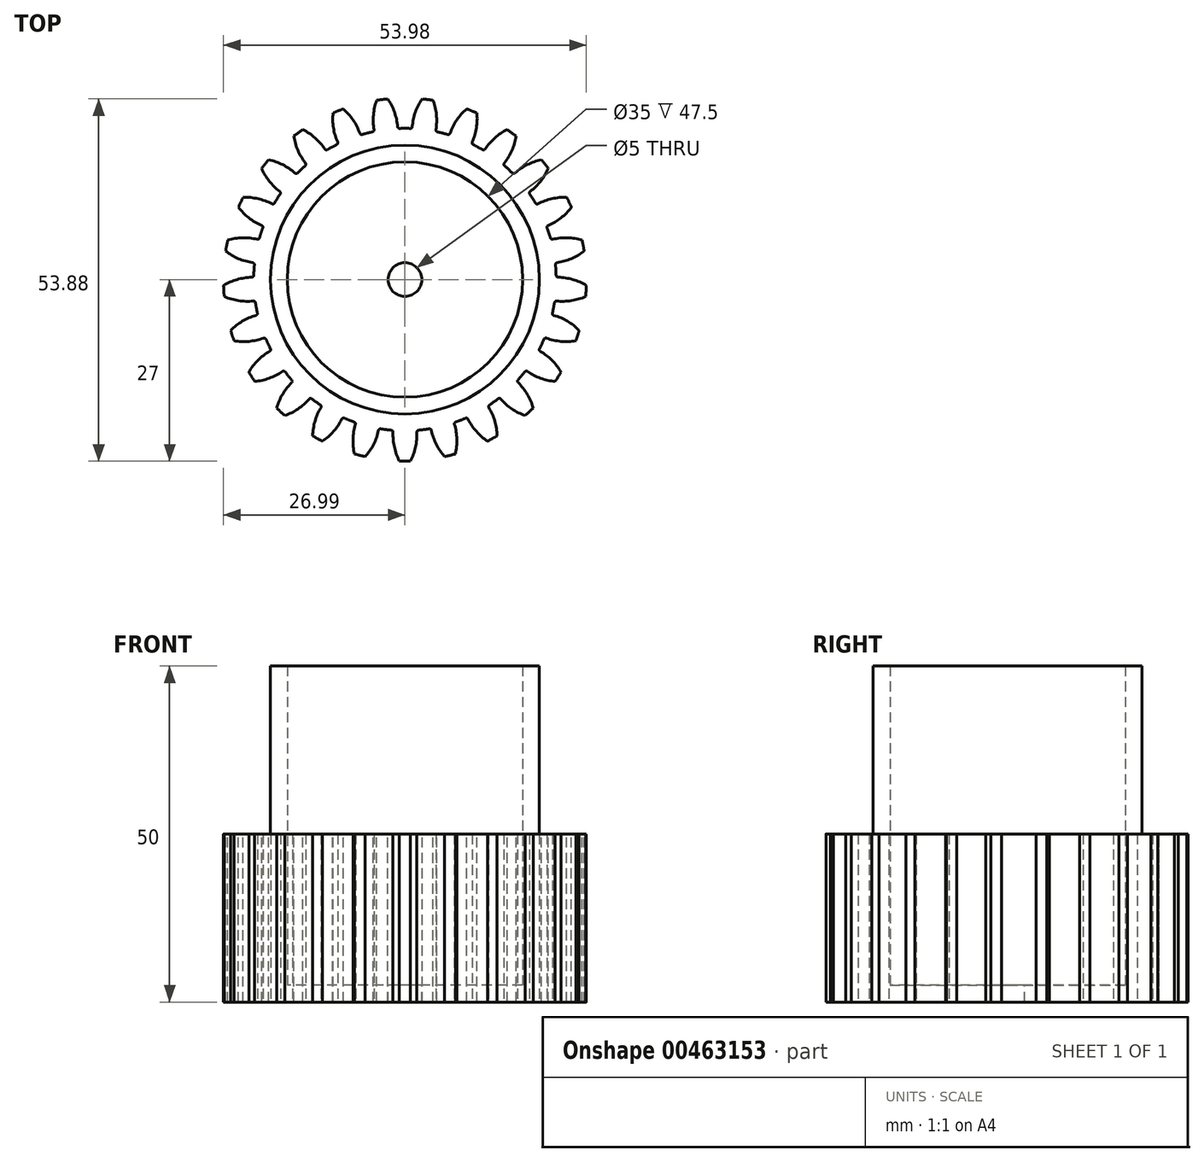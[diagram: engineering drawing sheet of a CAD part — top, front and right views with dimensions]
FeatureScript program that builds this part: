
annotation { "Feature Type Name" : "Feature", "Feature Type Description" : "" }
export const myFeature = defineFeature(function(context is Context, id is Id, definition is map)
    precondition{}
    {
        {
            var Q0;
            Q0=qCreatedBy(makeId("Top.planeOp"),FACE);
            var sketch = newSketch(context, id + "F0", { "sketchPlane" : qUnion([Q0])});
            skCircle(sketch, "E0", {"center": v(0, 0) * mm, "radius": 25 * mm});
            skCircle(sketch, "E1", {"center": v(0, 0) * mm, "radius": 27 * mm});
            skCircle(sketch, "E2", {"center": v(0, 0) * mm, "radius": 22.5 * mm});
            skSolve(sketch);
        }
        {
            var Q0;
            Q0=makeQuery(id+"F0.imprint","IMPRINT",FACE,{"disambiguationData":[TD([[makeQuery(id+"F0.imprint","IMPRINT",EDGE,{"derivedFrom":sQuery(id+"F0.wireOp",EDGE,"E2")}),1.0]])]});
            var Q1;
            Q1=makeQuery(id+"F0.imprint","IMPRINT",FACE,{"disambiguationData":[TD([[makeQuery(id+"F0.imprint","IMPRINT",EDGE,{"derivedFrom":sQuery(id+"F0.wireOp",EDGE,"E0")}),1.0]])]});
            var Q2;
            Q2=makeQuery(id+"F0.imprint","IMPRINT",FACE,{"disambiguationData":[TD([[makeQuery(id+"F0.imprint","IMPRINT",EDGE,{"derivedFrom":sQuery(id+"F0.wireOp",EDGE,"E0")}),-1.0]])]});
            extrude(context, id + "F1", {"entities" : qUnion([Q0, Q1, Q2]), "endBound" : BoundingType.SYMMETRIC, "depth" : 25 * mm});
        }
        {
            var Q0;
            Q0=qCreatedBy(makeId("Top.planeOp"),FACE);
            var sketch = newSketch(context, id + "F2", { "sketchPlane" : qUnion([Q0])});
            skLineSegment(sketch, "E3", {"start": v(0, 0) * mm, "end": v(0, 27) * mm, "construction": true});
            skArc(sketch, "E4", {"start": v(-1.07, 22.47) * mm, "mid": v(-1.72, 25.34) * mm, "end": v(-3.32, 27.8) * mm});
            skArc(sketch, "E5.MirrorCS", {"start": v(1.07, 22.47) * mm, "mid": v(1.72, 25.34) * mm, "end": v(3.32, 27.8) * mm});
            skArc(sketch, "E6.0", {"start": v(1.07, 22.47) * mm, "mid": v(0, 22.5) * mm, "end": v(-1.07, 22.47) * mm});
            skArc(sketch, "E7.0", {"start": v(3.32, 27.8) * mm, "mid": v(0, 28) * mm, "end": v(-3.32, 27.8) * mm});
            skLineSegment(sketch, "E8", {"start": v(-1.57, 24.95) * mm, "end": v(1.57, 24.95) * mm, "construction": true});
            skLineSegment(sketch, "E9", {"start": v(-1.07, 22.47) * mm, "end": v(0, 0) * mm, "construction": true});
            skLineSegment(sketch, "E10", {"start": v(0, 20.64) * mm, "end": v(-3.75, 30.95) * mm, "construction": true});
            skLineSegment(sketch, "E11", {"start": v(0, 0) * mm, "end": v(3.38, 26.79) * mm, "construction": true});
            skLineSegment(sketch, "E12", {"start": v(1.57, 24.95) * mm, "end": v(4.68, 24.56) * mm, "construction": true});
            skSolve(sketch);
        }
        {
            var Q0;
            Q0=makeQuery(id+"F2.imprint","IMPRINT",FACE,{"disambiguationData":[TD([[makeQuery(id+"F2.imprint","IMPRINT",EDGE,{"derivedFrom":sQuery(id+"F2.wireOp",EDGE,"E4")}),-1.0]])]});
            extrude(context, id + "F3", {"entities" : qUnion([Q0]), "operationType" : NewBodyOperationType.REMOVE, "endBound" : BoundingType.THROUGH_ALL, "oppositeDirection" : true, "depth" : 25 * mm, "hasSecondDirection" : true, "secondDirectionBound" : SecondDirectionBoundingType.THROUGH_ALL, "secondDirectionOppositeDirection" : false, "secondDirectionDepth" : 25 * mm});
        }
        {
            var Q0;
            Q0=makeQuery(id+"F3.boolean.opBoolean","COPY",EDGE,{"derivedFrom":makeQuery(id+"F3.opExtrude","SWEPT_EDGE",EDGE,{"disambiguationData":[OSD([sQuery(id+"F2.wireOp",EDGE,"E4"),sQuery(id+"F2.wireOp",EDGE,"E6.0")])]})});
            var Q1;
            Q1=makeQuery(id+"F3.boolean.opBoolean","COPY",EDGE,{"derivedFrom":makeQuery(id+"F3.opExtrude","SWEPT_EDGE",EDGE,{"disambiguationData":[OSD([sQuery(id+"F2.wireOp",EDGE,"E5.MirrorCS"),sQuery(id+"F2.wireOp",EDGE,"E6.0")])]})});
            fillet(context, id + "F4", {"entities" : qUnion([Q0, Q1]), "radius" : .3 * mm, "tangentPropagation" : true, "allowEdgeOverflow" : false});
        }
        {
            var Q0;
            Q0=qCreatedBy(makeId("Front.planeOp"),FACE);
            var sketch = newSketch(context, id + "F5", { "sketchPlane" : qUnion([Q0])});
            skLineSegment(sketch, "E13", {"start": v(0, 20.26) * mm, "end": v(0, -19.1) * mm, "construction": true});
            skSolve(sketch);
        }
        {
            var Q0;
            Q0=makeQuery(id+"F1.opExtrude","SWEPT_BODY",BODY,{"disambiguationData":[OSD([sQuery(id+"F0.wireOp",EDGE,"E1")])]});
            var Q1;
            Q1=sQuery(id+"F5.wireOp",EDGE,"E13");
            circularPattern(context, id + "F6", {"entities" : qUnion([Q0]), "axis" : qUnion([Q1]), "angle" : 360 * degree, "instanceCount" : 25, "equalSpace" : true});
        }
        {
            var Q0;
            Q0=makeQuery(id+"F1.opExtrude","SWEPT_BODY",BODY,{"disambiguationData":[OSD([sQuery(id+"F0.wireOp",EDGE,"E1")])]});
            var Q1;
            Q1=makeQuery(id+"F6.opPattern","COPY",BODY,{"derivedFrom":makeQuery(id+"F1.opExtrude","SWEPT_BODY",BODY,{"disambiguationData":[OSD([sQuery(id+"F0.wireOp",EDGE,"E1")])]}),"instanceName":"24"});
            var Q2;
            Q2=makeQuery(id+"F6.opPattern","COPY",BODY,{"derivedFrom":makeQuery(id+"F1.opExtrude","SWEPT_BODY",BODY,{"disambiguationData":[OSD([sQuery(id+"F0.wireOp",EDGE,"E1")])]}),"instanceName":"3"});
            var Q3;
            Q3=makeQuery(id+"F6.opPattern","COPY",BODY,{"derivedFrom":makeQuery(id+"F1.opExtrude","SWEPT_BODY",BODY,{"disambiguationData":[OSD([sQuery(id+"F0.wireOp",EDGE,"E1")])]}),"instanceName":"1"});
            var Q4;
            Q4=makeQuery(id+"F6.opPattern","COPY",BODY,{"derivedFrom":makeQuery(id+"F1.opExtrude","SWEPT_BODY",BODY,{"disambiguationData":[OSD([sQuery(id+"F0.wireOp",EDGE,"E1")])]}),"instanceName":"22"});
            var Q5;
            Q5=makeQuery(id+"F6.opPattern","COPY",BODY,{"derivedFrom":makeQuery(id+"F1.opExtrude","SWEPT_BODY",BODY,{"disambiguationData":[OSD([sQuery(id+"F0.wireOp",EDGE,"E1")])]}),"instanceName":"21"});
            var Q6;
            Q6=makeQuery(id+"F6.opPattern","COPY",BODY,{"derivedFrom":makeQuery(id+"F1.opExtrude","SWEPT_BODY",BODY,{"disambiguationData":[OSD([sQuery(id+"F0.wireOp",EDGE,"E1")])]}),"instanceName":"19"});
            var Q7;
            Q7=makeQuery(id+"F6.opPattern","COPY",BODY,{"derivedFrom":makeQuery(id+"F1.opExtrude","SWEPT_BODY",BODY,{"disambiguationData":[OSD([sQuery(id+"F0.wireOp",EDGE,"E1")])]}),"instanceName":"18"});
            var Q8;
            Q8=makeQuery(id+"F6.opPattern","COPY",BODY,{"derivedFrom":makeQuery(id+"F1.opExtrude","SWEPT_BODY",BODY,{"disambiguationData":[OSD([sQuery(id+"F0.wireOp",EDGE,"E1")])]}),"instanceName":"17"});
            var Q9;
            Q9=makeQuery(id+"F6.opPattern","COPY",BODY,{"derivedFrom":makeQuery(id+"F1.opExtrude","SWEPT_BODY",BODY,{"disambiguationData":[OSD([sQuery(id+"F0.wireOp",EDGE,"E1")])]}),"instanceName":"16"});
            var Q10;
            Q10=makeQuery(id+"F6.opPattern","COPY",BODY,{"derivedFrom":makeQuery(id+"F1.opExtrude","SWEPT_BODY",BODY,{"disambiguationData":[OSD([sQuery(id+"F0.wireOp",EDGE,"E1")])]}),"instanceName":"15"});
            var Q11;
            Q11=makeQuery(id+"F6.opPattern","COPY",BODY,{"derivedFrom":makeQuery(id+"F1.opExtrude","SWEPT_BODY",BODY,{"disambiguationData":[OSD([sQuery(id+"F0.wireOp",EDGE,"E1")])]}),"instanceName":"14"});
            var Q12;
            Q12=makeQuery(id+"F6.opPattern","COPY",BODY,{"derivedFrom":makeQuery(id+"F1.opExtrude","SWEPT_BODY",BODY,{"disambiguationData":[OSD([sQuery(id+"F0.wireOp",EDGE,"E1")])]}),"instanceName":"13"});
            var Q13;
            Q13=makeQuery(id+"F6.opPattern","COPY",BODY,{"derivedFrom":makeQuery(id+"F1.opExtrude","SWEPT_BODY",BODY,{"disambiguationData":[OSD([sQuery(id+"F0.wireOp",EDGE,"E1")])]}),"instanceName":"12"});
            var Q14;
            Q14=makeQuery(id+"F6.opPattern","COPY",BODY,{"derivedFrom":makeQuery(id+"F1.opExtrude","SWEPT_BODY",BODY,{"disambiguationData":[OSD([sQuery(id+"F0.wireOp",EDGE,"E1")])]}),"instanceName":"11"});
            var Q15;
            Q15=makeQuery(id+"F6.opPattern","COPY",BODY,{"derivedFrom":makeQuery(id+"F1.opExtrude","SWEPT_BODY",BODY,{"disambiguationData":[OSD([sQuery(id+"F0.wireOp",EDGE,"E1")])]}),"instanceName":"10"});
            var Q16;
            Q16=makeQuery(id+"F6.opPattern","COPY",BODY,{"derivedFrom":makeQuery(id+"F1.opExtrude","SWEPT_BODY",BODY,{"disambiguationData":[OSD([sQuery(id+"F0.wireOp",EDGE,"E1")])]}),"instanceName":"9"});
            var Q17;
            Q17=makeQuery(id+"F6.opPattern","COPY",BODY,{"derivedFrom":makeQuery(id+"F1.opExtrude","SWEPT_BODY",BODY,{"disambiguationData":[OSD([sQuery(id+"F0.wireOp",EDGE,"E1")])]}),"instanceName":"8"});
            var Q18;
            Q18=makeQuery(id+"F6.opPattern","COPY",BODY,{"derivedFrom":makeQuery(id+"F1.opExtrude","SWEPT_BODY",BODY,{"disambiguationData":[OSD([sQuery(id+"F0.wireOp",EDGE,"E1")])]}),"instanceName":"7"});
            var Q19;
            Q19=makeQuery(id+"F6.opPattern","COPY",BODY,{"derivedFrom":makeQuery(id+"F1.opExtrude","SWEPT_BODY",BODY,{"disambiguationData":[OSD([sQuery(id+"F0.wireOp",EDGE,"E1")])]}),"instanceName":"6"});
            var Q20;
            Q20=makeQuery(id+"F6.opPattern","COPY",BODY,{"derivedFrom":makeQuery(id+"F1.opExtrude","SWEPT_BODY",BODY,{"disambiguationData":[OSD([sQuery(id+"F0.wireOp",EDGE,"E1")])]}),"instanceName":"20"});
            var Q21;
            Q21=makeQuery(id+"F6.opPattern","COPY",BODY,{"derivedFrom":makeQuery(id+"F1.opExtrude","SWEPT_BODY",BODY,{"disambiguationData":[OSD([sQuery(id+"F0.wireOp",EDGE,"E1")])]}),"instanceName":"5"});
            var Q22;
            Q22=makeQuery(id+"F6.opPattern","COPY",BODY,{"derivedFrom":makeQuery(id+"F1.opExtrude","SWEPT_BODY",BODY,{"disambiguationData":[OSD([sQuery(id+"F0.wireOp",EDGE,"E1")])]}),"instanceName":"4"});
            var Q23;
            Q23=makeQuery(id+"F6.opPattern","COPY",BODY,{"derivedFrom":makeQuery(id+"F1.opExtrude","SWEPT_BODY",BODY,{"disambiguationData":[OSD([sQuery(id+"F0.wireOp",EDGE,"E1")])]}),"instanceName":"23"});
            var Q24;
            Q24=makeQuery(id+"F6.opPattern","COPY",BODY,{"derivedFrom":makeQuery(id+"F1.opExtrude","SWEPT_BODY",BODY,{"disambiguationData":[OSD([sQuery(id+"F0.wireOp",EDGE,"E1")])]}),"instanceName":"2"});
            booleanBodies(context, id + "F7", {"operationType" : BooleanOperationType.INTERSECTION, "tools" : qUnion([Q0, Q1, Q2, Q3, Q4, Q5, Q6, Q7, Q8, Q9, Q10, Q11, Q12, Q13, Q14, Q15, Q16, Q17, Q18, Q19, Q20, Q21, Q22, Q23, Q24])});
        }
        {
            var Q0;
            Q0=makeQuery(id+"F1.opExtrude","CAP_FACE",FACE,{"disambiguationData":[OSD([sQuery(id+"F0.wireOp",EDGE,"E1")])],"isStart":false});
            var sketch = newSketch(context, id + "F8", { "sketchPlane" : qUnion([Q0])});
            skCircle(sketch, "E14", {"center": v(0, 0) * mm, "radius": 20 * mm});
            skCircle(sketch, "E15", {"center": v(0, 0) * mm, "radius": 17.5 * mm});
            skCircle(sketch, "E16", {"center": v(0, 0) * mm, "radius": 2.5 * mm});
            skSolve(sketch);
        }
        {
            var Q0;
            Q0=makeQuery(id+"F8.imprint","IMPRINT",FACE,{"disambiguationData":[TD([[makeQuery(id+"F8.imprint","IMPRINT",EDGE,{"derivedFrom":sQuery(id+"F8.wireOp",EDGE,"E14")}),1.0]])]});
            extrude(context, id + "F9", {"entities" : qUnion([Q0]), "operationType" : NewBodyOperationType.ADD, "depth" : 25 * mm});
        }
        {
            var Q0;
            Q0=makeQuery(id+"F9.boolean.opBoolean","SPLIT",FACE,{"disambiguationData":[TD([makeQuery(id+"F9.opExtrude","SWEPT_FACE",FACE,{"disambiguationData":[OSD([sQuery(id+"F8.wireOp",EDGE,"E15")])]})])],"derivedFrom":makeQuery(id+"F1.opExtrude","CAP_FACE",FACE,{"disambiguationData":[OSD([sQuery(id+"F0.wireOp",EDGE,"E1")])],"isStart":false})});
            extrude(context, id + "F10", {"entities" : qUnion([Q0]), "operationType" : NewBodyOperationType.REMOVE, "oppositeDirection" : true, "depth" : 22.5 * mm});
        }
        {
            var Q0;
            Q0=makeQuery(id+"F8.imprint","IMPRINT",FACE,{"disambiguationData":[TD([[makeQuery(id+"F8.imprint","IMPRINT",EDGE,{"derivedFrom":sQuery(id+"F8.wireOp",EDGE,"E16")}),1.0]])]});
            extrude(context, id + "F11", {"entities" : qUnion([Q0]), "operationType" : NewBodyOperationType.REMOVE, "endBound" : BoundingType.THROUGH_ALL, "oppositeDirection" : true, "depth" : 25 * mm});
        }
    });
